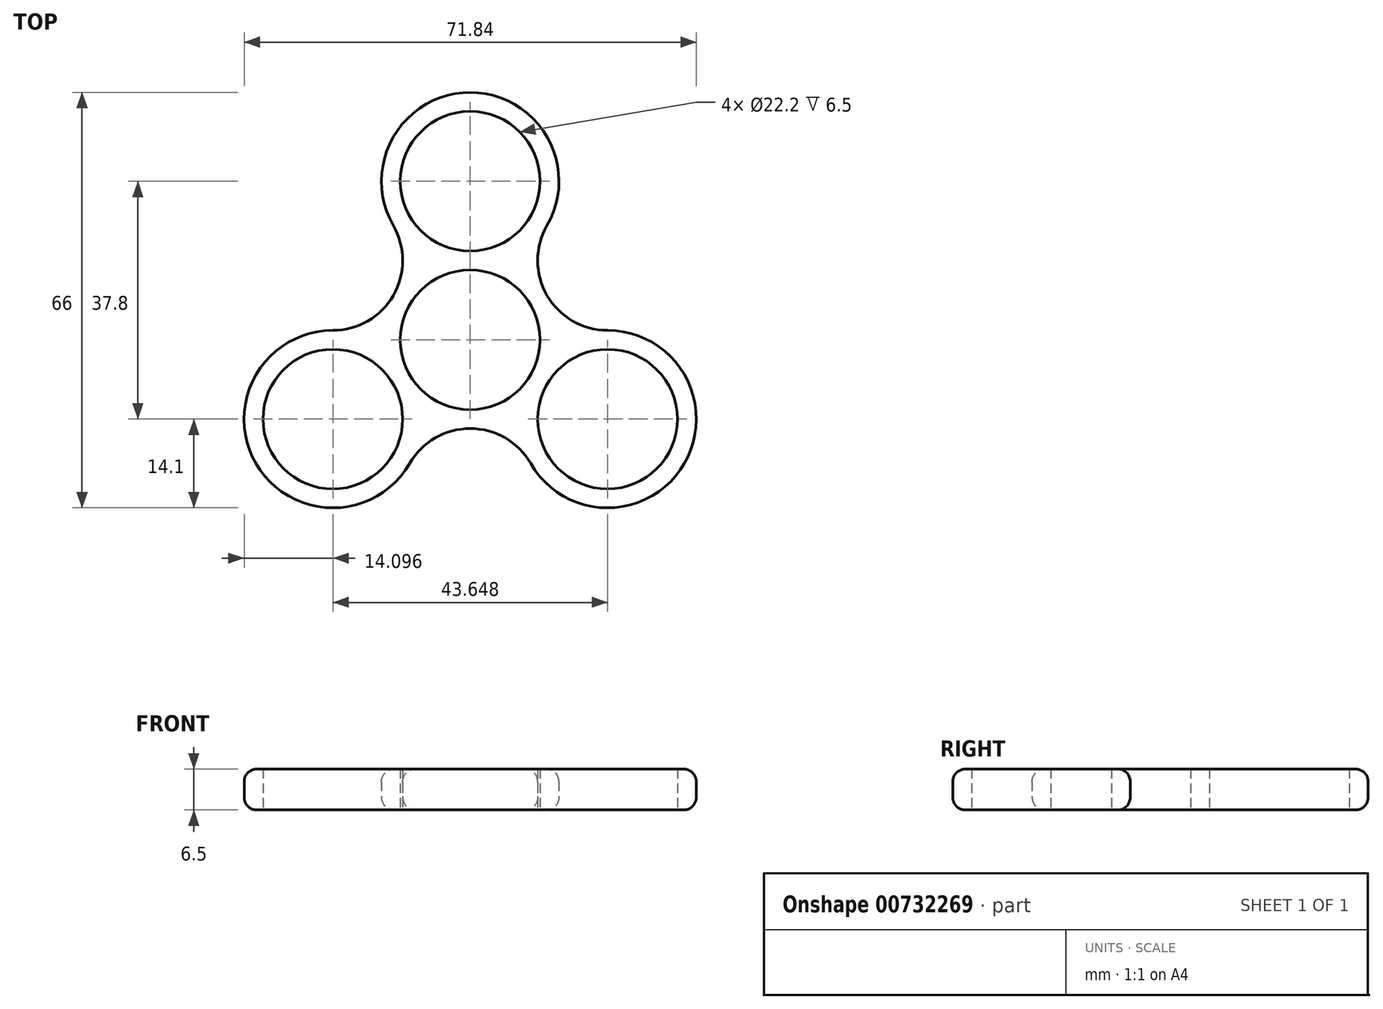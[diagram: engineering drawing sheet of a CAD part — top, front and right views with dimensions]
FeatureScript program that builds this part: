
annotation { "Feature Type Name" : "Feature", "Feature Type Description" : "" }
export const myFeature = defineFeature(function(context is Context, id is Id, definition is map)
    precondition{}
    {
        {
            var Q0;
            Q0=qCreatedBy(makeId("Top.planeOp"),FACE);
            var sketch = newSketch(context, id + "F0", { "sketchPlane" : qUnion([Q0])});
            skCircle(sketch, "E0", {"center": v(0, 0) * mm, "radius": 11.1 * mm});
            skLineSegment(sketch, "E1", {"start": v(0, 0) * mm, "end": v(0, 25.2) * mm});
            skCircle(sketch, "E2", {"center": v(0, 25.2) * mm, "radius": 11.1 * mm});
            skCircle(sketch, "E3.0", {"center": v(0, 25.2) * mm, "radius": 14.1 * mm});
            skCircle(sketch, "E4.0", {"center": v(0, 0) * mm, "radius": 14.1 * mm});
            skCircle(sketch, "E5.cCircle", {"center": v(0, 0) * mm, "radius": 25.2 * mm, "construction": true});
            skLineSegment(sketch, "E5.0", {"start": v(0, 25.2) * mm, "end": v(21.82, 12.6) * mm});
            skLineSegment(sketch, "E5.1", {"start": v(21.82, 12.6) * mm, "end": v(21.82, -12.6) * mm});
            skLineSegment(sketch, "E5.2", {"start": v(21.82, -12.6) * mm, "end": v(0, -25.2) * mm});
            skLineSegment(sketch, "E5.3", {"start": v(0, -25.2) * mm, "end": v(-21.82, -12.6) * mm});
            skLineSegment(sketch, "E5.4", {"start": v(-21.82, -12.6) * mm, "end": v(-21.82, 12.6) * mm});
            skLineSegment(sketch, "E5.5", {"start": v(-21.82, 12.6) * mm, "end": v(0, 25.2) * mm});
            skCircle(sketch, "E6", {"center": v(-21.82, -12.6) * mm, "radius": 11.1 * mm});
            skCircle(sketch, "E7", {"center": v(21.82, -12.6) * mm, "radius": 11.1 * mm});
            skCircle(sketch, "E8.0", {"center": v(21.82, -12.6) * mm, "radius": 14.1 * mm});
            skCircle(sketch, "E9.0", {"center": v(-21.82, -12.6) * mm, "radius": 14.1 * mm});
            skCircle(sketch, "E10", {"center": v(-21.82, 12.6) * mm, "radius": 11.1 * mm});
            skCircle(sketch, "E11", {"center": v(21.82, 12.6) * mm, "radius": 11.1 * mm});
            skCircle(sketch, "E12", {"center": v(0, -25.2) * mm, "radius": 11.1 * mm});
            skSolve(sketch);
        }
        {
            var Q0;
            {var subQ0=sQuery(id+"F0.wireOp",EDGE,"E5.5");var subQ1=sQuery(id+"F0.wireOp",EDGE,"E2");var subQ2=makeQuery(id+"F0.imprint","INTERSECT",VERTEX,{"derivedFrom":[subQ1,subQ0]});Q0=makeQuery(id+"F0.imprint","IMPRINT",FACE,{"disambiguationData":[TD([[makeQuery(id+"F0.imprint","IMPRINT",EDGE,{"disambiguationData":[TD([[subQ2,1.0]])],"derivedFrom":subQ1}),-1.0]])]});}
            var Q1;
            {var subQ0=sQuery(id+"F0.wireOp",EDGE,"E5.5");var subQ1=sQuery(id+"F0.wireOp",EDGE,"E2");var subQ2=makeQuery(id+"F0.imprint","INTERSECT",VERTEX,{"derivedFrom":[subQ1,subQ0]});Q1=makeQuery(id+"F0.imprint","IMPRINT",FACE,{"disambiguationData":[TD([[makeQuery(id+"F0.imprint","IMPRINT",EDGE,{"disambiguationData":[TD([[subQ2,-1.0]])],"derivedFrom":subQ1}),-1.0]])]});}
            var Q2;
            {var subQ0=sQuery(id+"F0.wireOp",EDGE,"E4.0");var subQ1=sQuery(id+"F0.wireOp",EDGE,"E3.0");var subQ2=makeQuery(id+"F0.imprint","INTERSECT",VERTEX,{"disambiguationData":[OD(0.0)],"derivedFrom":[subQ1,subQ0]});Q2=makeQuery(id+"F0.imprint","IMPRINT",FACE,{"disambiguationData":[TD([[makeQuery(id+"F0.imprint","IMPRINT",EDGE,{"disambiguationData":[TD([[subQ2,-1.0]])],"derivedFrom":subQ0}),-1.0]])]});}
            var Q3;
            {var subQ0=sQuery(id+"F0.wireOp",EDGE,"E4.0");var subQ4=sQuery(id+"F0.wireOp",EDGE,"E3.0");var subQ5=makeQuery(id+"F0.imprint","INTERSECT",VERTEX,{"disambiguationData":[OD(0.0)],"derivedFrom":[subQ4,subQ0]});Q3=makeQuery(id+"F0.imprint","IMPRINT",FACE,{"disambiguationData":[TD([[makeQuery(id+"F0.imprint","IMPRINT",EDGE,{"disambiguationData":[TD([[subQ5,-1.0]])],"derivedFrom":subQ0}),1.0]])]});}
            var Q4;
            {var subQ0=sQuery(id+"F0.wireOp",EDGE,"E10");var subQ1=sQuery(id+"F0.wireOp",EDGE,"E4.0");var subQ2=makeQuery(id+"F0.imprint","INTERSECT",VERTEX,{"derivedFrom":[subQ1,subQ0]});Q4=makeQuery(id+"F0.imprint","IMPRINT",FACE,{"disambiguationData":[TD([[makeQuery(id+"F0.imprint","IMPRINT",EDGE,{"disambiguationData":[TD([[subQ2,-1.0]])],"derivedFrom":subQ1}),-1.0]])]});}
            var Q5;
            {var subQ0=sQuery(id+"F0.wireOp",EDGE,"E9.0");var subQ1=sQuery(id+"F0.wireOp",EDGE,"E4.0");var subQ2=makeQuery(id+"F0.imprint","INTERSECT",VERTEX,{"disambiguationData":[OD(0.0)],"derivedFrom":[subQ1,subQ0]});Q5=makeQuery(id+"F0.imprint","IMPRINT",FACE,{"disambiguationData":[TD([[makeQuery(id+"F0.imprint","IMPRINT",EDGE,{"disambiguationData":[TD([[subQ2,-1.0]])],"derivedFrom":subQ1}),-1.0]])]});}
            var Q6;
            {var subQ0=sQuery(id+"F0.wireOp",EDGE,"E6");var subQ1=sQuery(id+"F0.wireOp",EDGE,"E5.3");var subQ2=makeQuery(id+"F0.imprint","INTERSECT",VERTEX,{"derivedFrom":[subQ1,subQ0]});Q6=makeQuery(id+"F0.imprint","IMPRINT",FACE,{"disambiguationData":[TD([[makeQuery(id+"F0.imprint","IMPRINT",EDGE,{"disambiguationData":[TD([[subQ2,1.0]])],"derivedFrom":subQ0}),-1.0]])]});}
            var Q7;
            {var subQ0=sQuery(id+"F0.wireOp",EDGE,"E6");var subQ1=sQuery(id+"F0.wireOp",EDGE,"E4.0");var subQ2=makeQuery(id+"F0.imprint","INTERSECT",VERTEX,{"derivedFrom":[subQ1,subQ0]});Q7=makeQuery(id+"F0.imprint","IMPRINT",FACE,{"disambiguationData":[TD([[makeQuery(id+"F0.imprint","IMPRINT",EDGE,{"disambiguationData":[TD([[subQ2,-1.0]])],"derivedFrom":subQ1}),-1.0]])]});}
            var Q8;
            {var subQ0=sQuery(id+"F0.wireOp",EDGE,"E9.0");var subQ1=sQuery(id+"F0.wireOp",EDGE,"E4.0");var subQ2=makeQuery(id+"F0.imprint","INTERSECT",VERTEX,{"disambiguationData":[OD(0.0)],"derivedFrom":[subQ1,subQ0]});Q8=makeQuery(id+"F0.imprint","IMPRINT",FACE,{"disambiguationData":[TD([[makeQuery(id+"F0.imprint","IMPRINT",EDGE,{"disambiguationData":[TD([[subQ2,-1.0]])],"derivedFrom":subQ1}),1.0]])]});}
            var Q9;
            {var subQ0=sQuery(id+"F0.wireOp",EDGE,"E9.0");var subQ1=sQuery(id+"F0.wireOp",EDGE,"E4.0");var subQ2=makeQuery(id+"F0.imprint","INTERSECT",VERTEX,{"disambiguationData":[OD(1.0)],"derivedFrom":[subQ1,subQ0]});Q9=makeQuery(id+"F0.imprint","IMPRINT",FACE,{"disambiguationData":[TD([[makeQuery(id+"F0.imprint","IMPRINT",EDGE,{"disambiguationData":[TD([[subQ2,-1.0]])],"derivedFrom":subQ1}),-1.0]])]});}
            var Q10;
            {var subQ0=sQuery(id+"F0.wireOp",EDGE,"E9.0");var subQ5=sQuery(id+"F0.wireOp",EDGE,"E0");var subQ8=makeQuery(id+"F0.imprint","INTERSECT",VERTEX,{"derivedFrom":[subQ5,subQ0]});Q10=makeQuery(id+"F0.imprint","IMPRINT",FACE,{"disambiguationData":[TD([[makeQuery(id+"F0.imprint","IMPRINT",EDGE,{"disambiguationData":[TD([[subQ8,-1.0]])],"derivedFrom":subQ5}),-1.0]])]});}
            var Q11;
            {var subQ0=sQuery(id+"F0.wireOp",EDGE,"E12");var subQ1=sQuery(id+"F0.wireOp",EDGE,"E4.0");var subQ2=makeQuery(id+"F0.imprint","INTERSECT",VERTEX,{"derivedFrom":[subQ1,subQ0]});Q11=makeQuery(id+"F0.imprint","IMPRINT",FACE,{"disambiguationData":[TD([[makeQuery(id+"F0.imprint","IMPRINT",EDGE,{"disambiguationData":[TD([[subQ2,-1.0]])],"derivedFrom":subQ1}),-1.0]])]});}
            var Q12;
            {var subQ0=sQuery(id+"F0.wireOp",EDGE,"E8.0");var subQ1=sQuery(id+"F0.wireOp",EDGE,"E4.0");var subQ2=makeQuery(id+"F0.imprint","INTERSECT",VERTEX,{"disambiguationData":[OD(0.0)],"derivedFrom":[subQ1,subQ0]});Q12=makeQuery(id+"F0.imprint","IMPRINT",FACE,{"disambiguationData":[TD([[makeQuery(id+"F0.imprint","IMPRINT",EDGE,{"disambiguationData":[TD([[subQ2,-1.0]])],"derivedFrom":subQ1}),-1.0]])]});}
            var Q13;
            {var subQ0=sQuery(id+"F0.wireOp",EDGE,"E8.0");var subQ1=sQuery(id+"F0.wireOp",EDGE,"E4.0");var subQ2=makeQuery(id+"F0.imprint","INTERSECT",VERTEX,{"disambiguationData":[OD(0.0)],"derivedFrom":[subQ1,subQ0]});Q13=makeQuery(id+"F0.imprint","IMPRINT",FACE,{"disambiguationData":[TD([[makeQuery(id+"F0.imprint","IMPRINT",EDGE,{"disambiguationData":[TD([[subQ2,-1.0]])],"derivedFrom":subQ1}),1.0]])]});}
            var Q14;
            {var subQ0=sQuery(id+"F0.wireOp",EDGE,"E7");var subQ1=sQuery(id+"F0.wireOp",EDGE,"E4.0");var subQ2=makeQuery(id+"F0.imprint","INTERSECT",VERTEX,{"derivedFrom":[subQ1,subQ0]});Q14=makeQuery(id+"F0.imprint","IMPRINT",FACE,{"disambiguationData":[TD([[makeQuery(id+"F0.imprint","IMPRINT",EDGE,{"disambiguationData":[TD([[subQ2,-1.0]])],"derivedFrom":subQ1}),-1.0]])]});}
            var Q15;
            {var subQ0=sQuery(id+"F0.wireOp",EDGE,"E7");var subQ1=sQuery(id+"F0.wireOp",EDGE,"E5.1");var subQ2=makeQuery(id+"F0.imprint","INTERSECT",VERTEX,{"derivedFrom":[subQ1,subQ0]});Q15=makeQuery(id+"F0.imprint","IMPRINT",FACE,{"disambiguationData":[TD([[makeQuery(id+"F0.imprint","IMPRINT",EDGE,{"disambiguationData":[TD([[subQ2,1.0]])],"derivedFrom":subQ0}),-1.0]])]});}
            var Q16;
            {var subQ0=sQuery(id+"F0.wireOp",EDGE,"E11");var subQ1=sQuery(id+"F0.wireOp",EDGE,"E4.0");var subQ2=makeQuery(id+"F0.imprint","INTERSECT",VERTEX,{"derivedFrom":[subQ1,subQ0]});Q16=makeQuery(id+"F0.imprint","IMPRINT",FACE,{"disambiguationData":[TD([[makeQuery(id+"F0.imprint","IMPRINT",EDGE,{"disambiguationData":[TD([[subQ2,1.0]])],"derivedFrom":subQ1}),-1.0]])]});}
            var Q17;
            {var subQ0=sQuery(id+"F0.wireOp",EDGE,"E4.0");var subQ4=sQuery(id+"F0.wireOp",EDGE,"E3.0");var subQ5=makeQuery(id+"F0.imprint","INTERSECT",VERTEX,{"disambiguationData":[OD(1.0)],"derivedFrom":[subQ4,subQ0]});Q17=makeQuery(id+"F0.imprint","IMPRINT",FACE,{"disambiguationData":[TD([[makeQuery(id+"F0.imprint","IMPRINT",EDGE,{"disambiguationData":[TD([[subQ5,1.0]])],"derivedFrom":subQ0}),1.0]])]});}
            var Q18;
            {var subQ0=sQuery(id+"F0.wireOp",EDGE,"E4.0");var subQ1=sQuery(id+"F0.wireOp",EDGE,"E3.0");var subQ2=makeQuery(id+"F0.imprint","INTERSECT",VERTEX,{"disambiguationData":[OD(1.0)],"derivedFrom":[subQ1,subQ0]});Q18=makeQuery(id+"F0.imprint","IMPRINT",FACE,{"disambiguationData":[TD([[makeQuery(id+"F0.imprint","IMPRINT",EDGE,{"disambiguationData":[TD([[subQ2,1.0]])],"derivedFrom":subQ0}),-1.0]])]});}
            var Q19;
            {var subQ0=sQuery(id+"F0.wireOp",EDGE,"E5.0");var subQ1=sQuery(id+"F0.wireOp",EDGE,"E2");var subQ2=makeQuery(id+"F0.imprint","INTERSECT",VERTEX,{"derivedFrom":[subQ1,subQ0]});Q19=makeQuery(id+"F0.imprint","IMPRINT",FACE,{"disambiguationData":[TD([[makeQuery(id+"F0.imprint","IMPRINT",EDGE,{"disambiguationData":[TD([[subQ2,1.0]])],"derivedFrom":subQ1}),-1.0]])]});}
            var Q20;
            {var subQ0=sQuery(id+"F0.wireOp",EDGE,"E3.0");var subQ3=sQuery(id+"F0.wireOp",EDGE,"E4.0");var subQ5=makeQuery(id+"F0.imprint","INTERSECT",VERTEX,{"disambiguationData":[OD(1.0)],"derivedFrom":[subQ0,subQ3]});Q20=makeQuery(id+"F0.imprint","IMPRINT",FACE,{"disambiguationData":[TD([[makeQuery(id+"F0.imprint","IMPRINT",EDGE,{"disambiguationData":[TD([[subQ5,1.0]])],"derivedFrom":subQ0}),1.0]])]});}
            var Q21;
            {var subQ0=sQuery(id+"F0.wireOp",EDGE,"E3.0");var subQ3=sQuery(id+"F0.wireOp",EDGE,"E4.0");var subQ5=makeQuery(id+"F0.imprint","INTERSECT",VERTEX,{"disambiguationData":[OD(0.0)],"derivedFrom":[subQ0,subQ3]});Q21=makeQuery(id+"F0.imprint","IMPRINT",FACE,{"disambiguationData":[TD([[makeQuery(id+"F0.imprint","IMPRINT",EDGE,{"disambiguationData":[TD([[subQ5,-1.0]])],"derivedFrom":subQ0}),1.0]])]});}
            extrude(context, id + "F1", {"entities" : qUnion([Q0, Q1, Q2, Q3, Q4, Q5, Q6, Q7, Q8, Q9, Q10, Q11, Q12, Q13, Q14, Q15, Q16, Q17, Q18, Q19, Q20, Q21]), "depth" : 6.5 * mm, "offsetDistance" : 25 * mm});
        }
        {
            var Q0;
            Q0=makeQuery(id+"F1.opExtrude","CAP_EDGE",EDGE,{"disambiguationData":[OSD([sQuery(id+"F0.wireOp",EDGE,"E12")])],"isStart":false});
            var Q1;
            Q1=makeQuery(id+"F1.opExtrude","CAP_EDGE",EDGE,{"disambiguationData":[OSD([sQuery(id+"F0.wireOp",EDGE,"E12")])],"isStart":true});
            fillet(context, id + "F2", {"entities" : qUnion([Q0, Q1]), "radius" : 2 * mm, "tangentPropagation" : true, "allowEdgeOverflow" : false});
        }
    });
